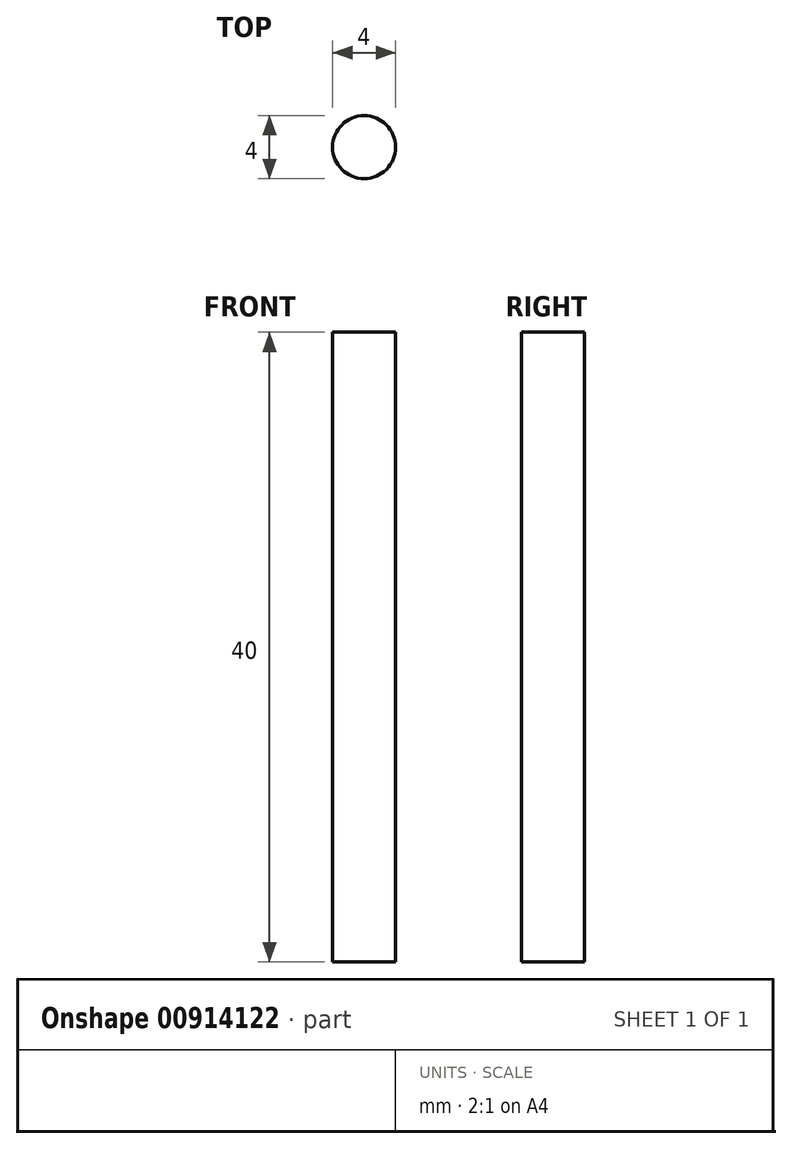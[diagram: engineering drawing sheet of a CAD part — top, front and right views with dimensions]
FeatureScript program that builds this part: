
annotation { "Feature Type Name" : "Feature", "Feature Type Description" : "" }
export const myFeature = defineFeature(function(context is Context, id is Id, definition is map)
    precondition{}
    {
        {
            var Q0;
            Q0=qCreatedBy(makeId("Top.planeOp"),FACE);
            var sketch = newSketch(context, id + "F0", { "sketchPlane" : qUnion([Q0])});
            skCircle(sketch, "E0", {"center": v(0, 0) * mm, "radius": 2 * mm});
            skSolve(sketch);
        }
        {
            var Q0;
            Q0 = qSketchRegion(id + "F0", true);
            extrude(context, id + "F1", {"entities" : qUnion([Q0]), "depth" : 40 * mm, "offsetDistance" : 25 * mm});
        }
    });
